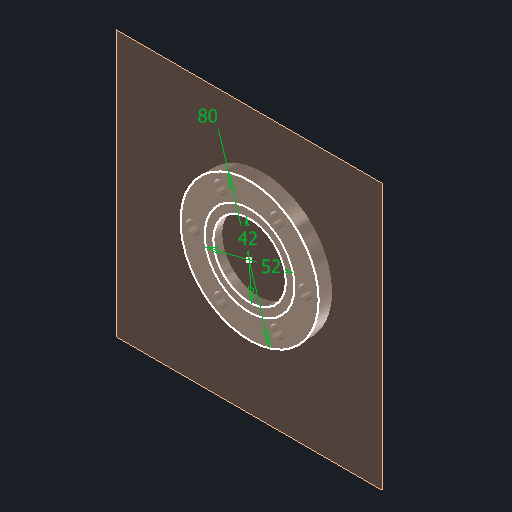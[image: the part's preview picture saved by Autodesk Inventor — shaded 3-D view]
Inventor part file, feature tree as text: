
AUTODESK INVENTOR PART (.ipt)
format: ipt  version: 2022 (Build 260153000, 153)  size: 135,680 bytes
history: native  units: mm
features: sketch x2, extrude x2, other x2, plane x1, hole x1
ambient origin geometry x8: Origin, YZ Plane, XZ Plane, XY Plane, X Axis, Y Axis, Z Axis, Center Point
bodies: Solid1 (feature_tree)
feature tree (8):
  plane  "Work Plane1"
  sketch  "Sketch1"  dims[d0=52.0mm d1=80.0mm]
  extrude  "Extrusion1"  Depth=80.0mm
  extrude  "Extrusion2"  Depth=8.0mm
  hole  "Hole1"  [1 undecoded]
  sketch  "Sketch2"  dims[d2=5.5mm d3=0.0mm d4=42.0mm d5=8.0mm d6=0.0mm d7=65.0mm d8=60.0mm d10=360.0deg d12=4.5mm d13=6.0mm d14=8.0mm d15=4.6mm d16=14.3117mm d17=8.0mm d18=20.594885mm]
  other  "SistemaDeElevación.iam"
  other  "soporte de rodamientos:1"
note: 1 required parameter value undecoded (feature->parameter linkage not recoverable at this tier; creation-order binding heuristic only, values carry confidence <= 0.55)
